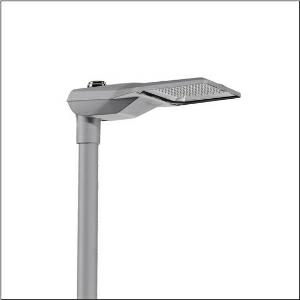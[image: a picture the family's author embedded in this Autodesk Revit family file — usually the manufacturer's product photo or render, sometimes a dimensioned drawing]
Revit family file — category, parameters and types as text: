
# Revit family: streetlight_sl_21_midi___st1_5a_5xe7p47n08mb_d352
name_source: partatom
category: Lighting Fixtures
units: mm (PartAtom-declared; Revit-internal decimal feet)

## family parameters
Cut with Voids When Loaded = No
Host = Face
Light Source = No
Part Type = Normal
Room Calculation Point = No
Round Connector Dimension = Use Diameter
Shared = No

## types (1)
- --- (1 x LED, 19830 lm, 147 W, 4000K)
    Apparent Load = 147 VA
    CIE Flux Codes = 22 53 95 100 100
    Color Rendering = 70
    Color Temperature = 4000K
    Default Elevation = 1800 mm
    Description = Streetlight SL 21 midi, mast luminaire, primary light control with lens, of PMMA, primary optical cover: cover, of toughened safety glass, transparent, light distribution: ST1.5a, light emission: direct distribution, primary light characteristic: asymmetric, installation type: side-entry, LED, 3G 2.5mm², High Power LED, rated luminous flux: 19.830lm, luminous efficacy: 135lm/W, light colour: 740, colour temperature: 4000K, control gear: NEMA (7pin), control: overheat protection, pre-setting: linear dimming characteristic, constant luminous flux control, time-dependent luminous flux control, flexible luminous flux parameterisation, mains connection: 220..240V, AC, 50/60Hz, connection cable pre-assembled, cable length: 12,5m, wiring characteristics: H05VV-F, start of lifetime: 147W, end of service life: 155W, reduction: 65W, luminaire housing, of diecast aluminium (EN AC-44300), powder-coated, SITECO metallic grey (DB 702S), corrosivity category C5 high according to DIN EN ISO 12944, multi-level sealing system, sealing non-destructively replaceable, inclination adjustable: 0°, 5°, 10°, 15°, length: 644mm, width: 335mm, height: 110mm, spigot size: 42mm (side-entry), mounting height: 4..8m, protection rating (complete): IP66, insulation class (complete): insulation class I (protective earthing), certification: CE, ENEC, ENEC+, VDE, impact resistance: IK10, permissible operating ambient temperature for outdoor applications: -40..+50°C, standard-compliant lighting for roads and squares, packaging unit: 1 piece

Light Distribution: ST1.5a
    Height = 111 mm
    Lamp = 1 x LED
    Lamp Light Flux = 19830 lm
    Lamp Power = 147 W
    Lamp count = 1
    Length = 644 mm
    Luminous efficacy = 135 lm/W
    Manufacturer = Siteco
    ModVariant = No
    Model = 5XE7P47N08MB
    Number of Poles = 1
    OnlyDefault = Yes
    Power Factor = 1
    Product Name = Streetlight SL 21 midi | ST1.5a
    Product group = mast luminaire | pylon top
    ProductGroupID = 6100
    Protection Class = Protection class I
    Protection Degree = IP 66
    RLX_Detail_Level = 1
    RLX_Emergency_Light_Flux = 0 lm
    RLX_Emergency_Type = 0
    RLX_Emergency_Type_DB = No
    RlxData = <blob elided: 30045 chars, md5=8d3d4b5e>
    Socket = socket
    Standby Power = 0 W
    System Light Flux = 19830 lm
    System Power = 147 W
    Type Comments = factory setting: luminous flux: 100 % | dim-lin: 254 | 750 mA
    Type Image = l_1294377.jpg
    URL = http://relux.com
    VarID = @adj_132879
    Voltage = 0 V
    Weight = 0.00 kg
    Width = 336 mm

## geometry (parser evidence)
native form markers: Blend x4, Sweep x8
no freeform markers — native parametric forms only
